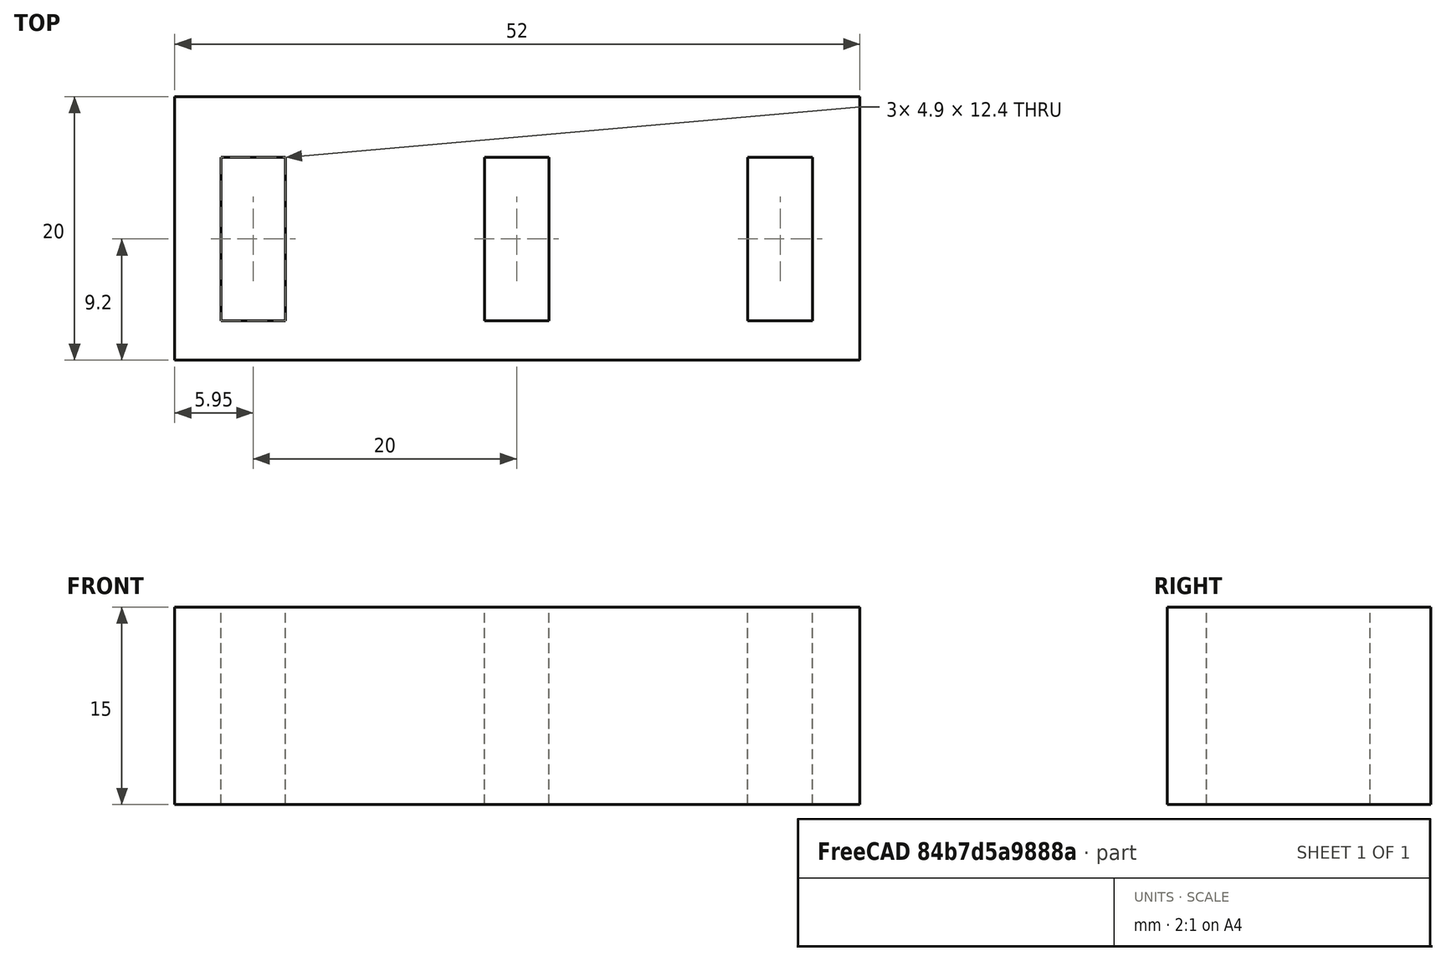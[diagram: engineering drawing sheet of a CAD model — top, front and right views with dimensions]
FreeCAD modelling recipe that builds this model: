
FCSTD DOCUMENT  (FreeCAD 0.20R29177 +233 (Git))
Label: porta_pendrives
License: All rights reserved
LicenseURL: http://en.wikipedia.org/wiki/All_rights_reserved
objects: Part::Box×4, Part::Cut×3
note: 7 computed .brp shape members not serialized (recipe doc carries the construction recipe); baked Part::Feature solids carry a one-line shape summary decoded from their .brp

FEATURE [Part::Box] Box  label="Cubo"
  AttacherType = Attacher::AttachEngine3D
  Height = 15
  Length = 52
  Width = 20
FEATURE [Part::Box] Box001  label="Cubo001"
  AttacherType = Attacher::AttachEngine3D
  Height = 16
  Length = 4.9
  Placement = pos=(3.5,3,0) rot=(0,0,1;0rad)
  Width = 12.4
FEATURE [Part::Box] Box002  label="Cubo002"
  AttacherType = Attacher::AttachEngine3D
  Height = 16
  Length = 4.9
  Placement = pos=(43.5,3,0) rot=(0,0,1;0rad)
  Width = 12.4
FEATURE [Part::Box] Box003  label="Cubo003"
  AttacherType = Attacher::AttachEngine3D
  Height = 16
  Length = 4.9
  Placement = pos=(23.5,3,0) rot=(0,0,1;0rad)
  Width = 12.4
FEATURE [Part::Cut] Cut
  Base = -> Box
  Tool = -> Box001
FEATURE [Part::Cut] Cut001
  Base = -> Cut
  Tool = -> Box003
FEATURE [Part::Cut] Cut002
  Base = -> Cut001
  Tool = -> Box002
